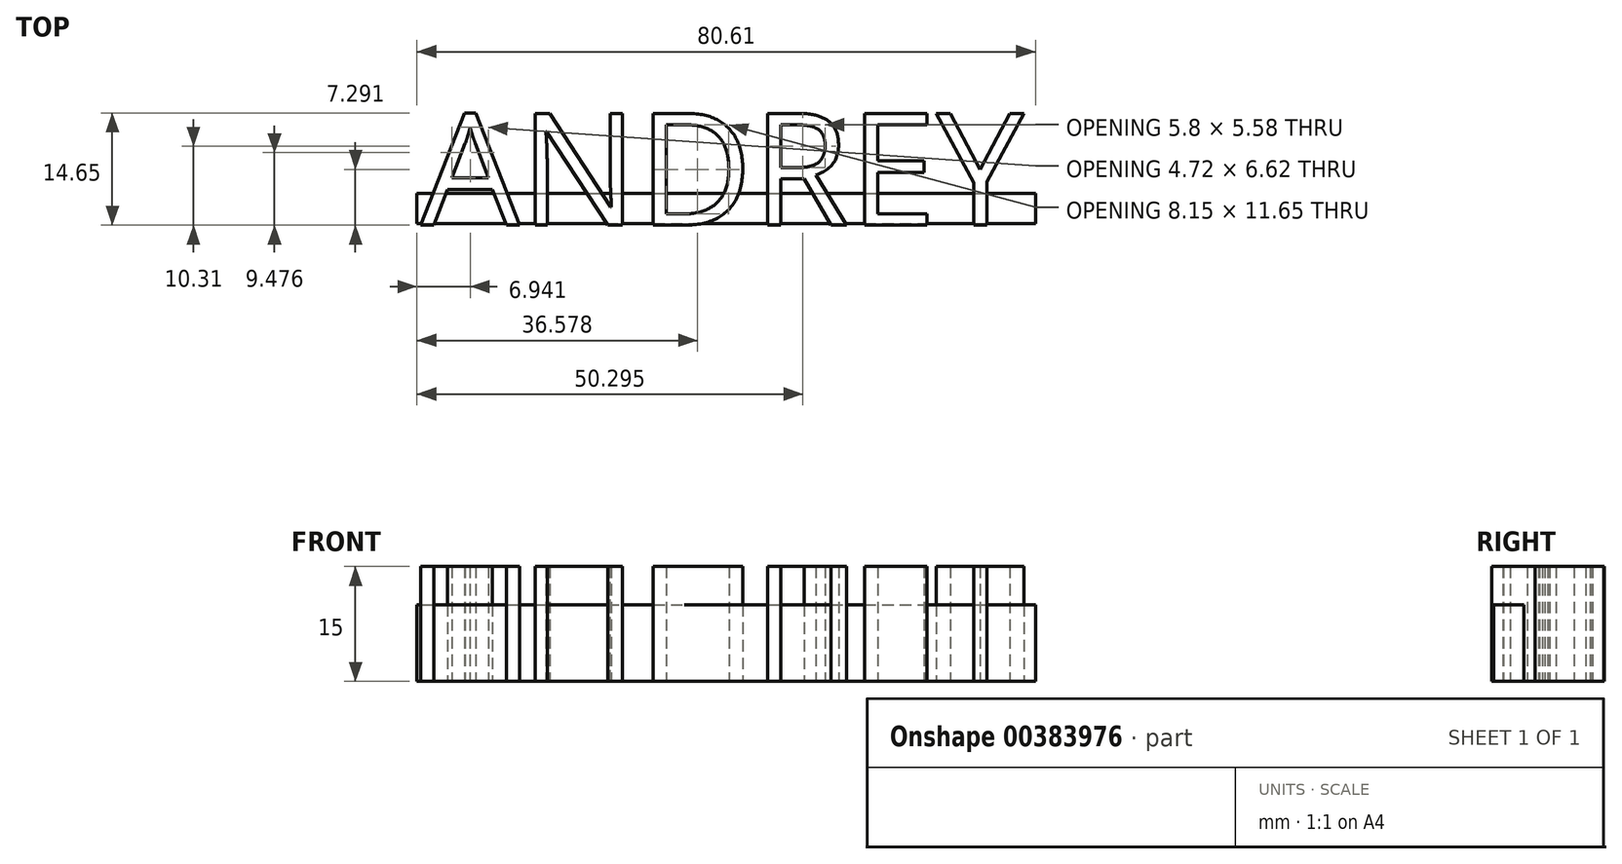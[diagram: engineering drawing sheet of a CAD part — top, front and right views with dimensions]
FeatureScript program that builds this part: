
annotation { "Feature Type Name" : "Feature", "Feature Type Description" : "" }
export const myFeature = defineFeature(function(context is Context, id is Id, definition is map)
    precondition{}
    {
        {
            var Q0;
            Q0=qCreatedBy(makeId("Top.planeOp"),FACE);
            var sketch = newSketch(context, id + "F0", { "sketchPlane" : qUnion([Q0])});
            skText(sketch, "E0", { "text": "ANDREY", "fontName": "OpenSans-Regular.ttf"});
            const initialGuessF0  = {"E0": [-0.04845, 0.0287, 1, 0, 0.01471]};
            skSetInitialGuess(sketch, initialGuessF0);
            skSolve(sketch);
        }
        {
            var Q0;
            Q0=qCreatedBy(makeId("Top.planeOp"),FACE);
            var sketch = newSketch(context, id + "F1", { "sketchPlane" : qUnion([Q0])});
            skLineSegment(sketch, "E1.bottom", {"start": v(-48.92, 32.88) * mm, "end": v(31.69, 32.88) * mm});
            skLineSegment(sketch, "E1.top", {"start": v(-48.92, 28.91) * mm, "end": v(31.69, 28.91) * mm});
            skLineSegment(sketch, "E1.left", {"start": v(-48.92, 32.88) * mm, "end": v(-48.92, 28.91) * mm});
            skLineSegment(sketch, "E1.right", {"start": v(31.69, 32.88) * mm, "end": v(31.69, 28.91) * mm});
            skSolve(sketch);
        }
        {
            var Q0;
            Q0 = qSketchRegion(id + "F0", true);
            extrude(context, id + "F2", {"entities" : qUnion([Q0]), "depth" : 15 * mm});
        }
        {
            var Q0;
            Q0 = qSketchRegion(id + "F1", true);
            extrude(context, id + "F3", {"entities" : qUnion([Q0]), "depth" : 10 * mm});
        }
    });
